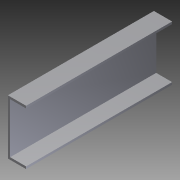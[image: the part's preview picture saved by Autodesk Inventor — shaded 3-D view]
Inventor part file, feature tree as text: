
AUTODESK INVENTOR PART (.ipt)
format: ipt  version: 2012 (Build 160160000, 160)  size: 77,312 bytes
history: native  units: in
note: dims shown in document units (in); Inventor stores cm internally (conversion verified against a paired STEP export)
features: extrude x1, sketch x1
ambient origin geometry x8: Origin, YZ Plane, XZ Plane, XY Plane, X Axis, Y Axis, Z Axis, Center Point
bodies: Solid1 (feature_tree)
feature tree (2):
  extrude  "Extrusion1"  Depth=1.0in
  sketch  "Sketch1"  dims[d0=3.0in d1=1.0in d2=0.125in d3=0.125in d4=0.125in d5=8.0in d6=0.0in]
